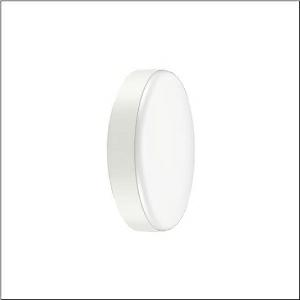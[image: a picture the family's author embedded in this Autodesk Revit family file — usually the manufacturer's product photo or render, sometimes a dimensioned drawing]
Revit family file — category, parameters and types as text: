
# Revit family: round_31_51wc10db44a
name_source: partatom
category: Lighting Fixtures
units: mm (PartAtom-declared; Revit-internal decimal feet)

## family parameters
Cut with Voids When Loaded = No
Host = Face
Light Source = No
Part Type = Normal
Room Calculation Point = No
Round Connector Dimension = Use Diameter
Shared = No

## types (1)
- Round 31 (1 x LED, 4400 lm, 34 W, 4000K)
    Apparent Load = 34 VA
    CIE Flux Codes = 44 75 94 94 100
    Color Rendering = 80
    Color Temperature = 4000K
    Default Elevation = 1800 mm
    Description = Round 31, wall and ceiling luminaire, primary optical cover: cover, of PC, opal, light emission: direct distribution, primary light characteristic: symmetric, installation type: surface-mounted, LED, rated luminous flux: 4.400lm, luminous efficacy: 129lm/W, light colour: 840, colour temperature: 4000K, control gear: DALI 2, with terminal, 3-pole, max. 2.5mm², mains connection: 220..240V, AC, 50/60Hz, rated input power: 34W, luminaire housing, of PC, traffic white (RAL 9016), diameter: 480mm, protection rating (complete): IP65, insulation class (complete): insulation class II (safety insulation), certification: CE, impact resistance: IK10, permissible operating ambient temperature: -20..+40°C, permissible storage temperature: -20..+60°C, packaging unit: 1 piece
    Height = 97 mm
    Lamp = 1 x LED
    Lamp Light Flux = 4400 lm
    Lamp Power = 34 W
    Lamp count = 1
    Length = 480 mm
    Luminous efficacy = 129 lm/W
    Manufacturer = Siteco
    ModVariant = No
    Model = 51WC10DB44A
    Mounting Place = Wall
    Mounting Type = Surface mounted
    Number of Poles = 1
    OnlyDefault = Yes
    Power Factor = 1
    Product Name = Round 31
    Product group = wall and ceiling luminaire | wall mounted
    ProductGroupID = 2001
    Protection Class = Protection class II
    Protection Degree = IP 65
    RLX_Detail_Level = 1
    RLX_Emergency_Light_Flux = 0 lm
    RLX_Emergency_Type = 0
    RLX_Emergency_Type_DB = No
    RlxData = <blob elided: 55269 chars, md5=08ba40d0>
    Socket = socket
    Standby Power = 0 W
    System Light Flux = 4400 lm
    System Power = 34 W
    Type Comments = Product without accessories
    Type Image = l_1007188.jpg
    URL = http://relux.com
    VarID = ---
    Voltage = 0 V
    Weight = 0.00 kg
    Width = 0 mm  [stored 0 ft]

note: [stored X ft] marks values corroborated as IEEE doubles in the binary element streams (Revit-internal decimal feet)

## geometry (parser evidence)
native form markers: Blend x4, Sweep x12
no freeform markers — native parametric forms only
